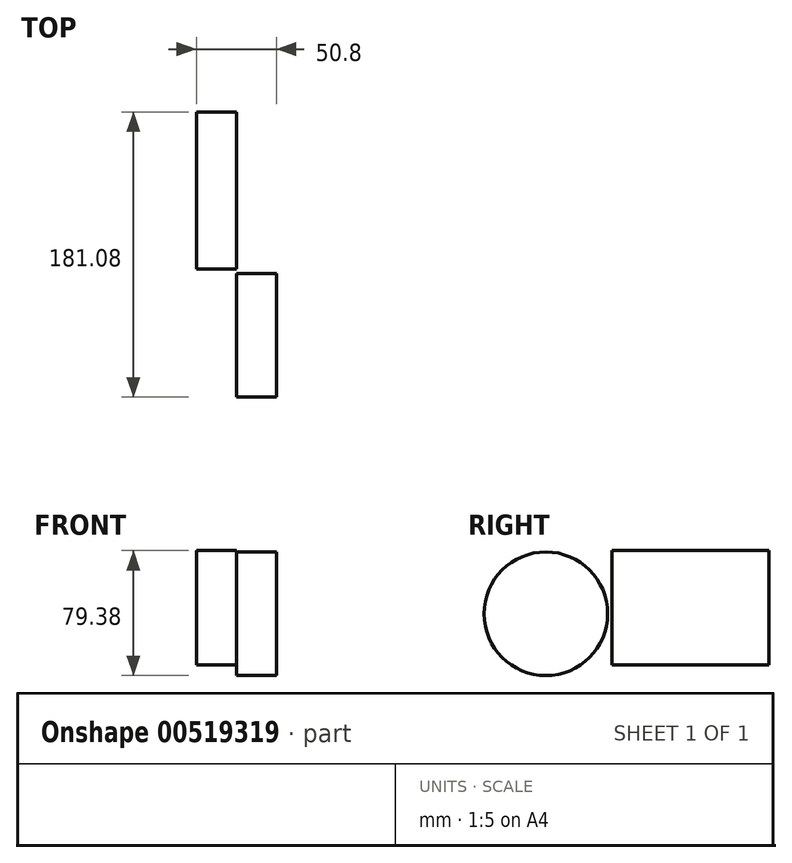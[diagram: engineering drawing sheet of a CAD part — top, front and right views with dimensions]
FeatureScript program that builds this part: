
annotation { "Feature Type Name" : "Feature", "Feature Type Description" : "" }
export const myFeature = defineFeature(function(context is Context, id is Id, definition is map)
    precondition{}
    {
        {
            var Q0;
            Q0=qCreatedBy(makeId("Right.planeOp"),FACE);
            var sketch = newSketch(context, id + "F0", { "sketchPlane" : qUnion([Q0])});
            skLineSegment(sketch, "E0", {"start": v(-51.33, 40.12) * mm, "end": v(48.41, 40.12) * mm});
            skLineSegment(sketch, "E1", {"start": v(48.41, 40.12) * mm, "end": v(48.41, -32.64) * mm});
            skLineSegment(sketch, "E2", {"start": v(-51.33, 40.12) * mm, "end": v(-51.33, -32.64) * mm});
            skLineSegment(sketch, "E3", {"start": v(-51.33, -32.64) * mm, "end": v(48.41, -32.64) * mm});
            skCircle(sketch, "E4", {"center": v(0, 0) * mm, "radius": 32.51 * mm});
            skSolve(sketch);
        }
        {
            var Q0;
            Q0=makeQuery(id+"F0.imprint","IMPRINT",FACE,{"disambiguationData":[TD([[makeQuery(id+"F0.imprint","IMPRINT",EDGE,{"derivedFrom":sQuery(id+"F0.wireOp",EDGE,"E4")}),1.0]])]});
            var Q1;
            Q1=makeQuery(id+"F0.imprint","IMPRINT",FACE,{"disambiguationData":[TD([[makeQuery(id+"F0.imprint","IMPRINT",EDGE,{"derivedFrom":sQuery(id+"F0.wireOp",EDGE,"E0")}),-1.0]])]});
            extrude(context, id + "F1", {"entities" : qUnion([Q0, Q1]), "depth" : 25.4 * mm, "offsetDistance" : 25.4 * mm});
        }
        {
            var Q0;
            Q0=makeQuery(id+"F1.opExtrude","CAP_FACE",FACE,{"disambiguationData":[OSD([sQuery(id+"F0.wireOp",EDGE,"E0"),sQuery(id+"F0.wireOp",EDGE,"E1"),sQuery(id+"F0.wireOp",EDGE,"E2"),sQuery(id+"F0.wireOp",EDGE,"E3")])],"isStart":false});
            var sketch = newSketch(context, id + "F2", { "sketchPlane" : qUnion([Q0])});
            skCircle(sketch, "E5", {"center": v(-93.4, 0) * mm, "radius": 39.26 * mm});
            skSolve(sketch);
        }
        {
            var Q0;
            Q0=makeQuery(id+"F2.imprint","IMPRINT",FACE,{"disambiguationData":[TD([[makeQuery(id+"F2.imprint","IMPRINT",EDGE,{"derivedFrom":sQuery(id+"F2.wireOp",EDGE,"E5")}),1.0]])]});
            extrude(context, id + "F3", {"entities" : qUnion([Q0]), "depth" : 25.4 * mm, "offsetDistance" : 25.4 * mm});
        }
    });
